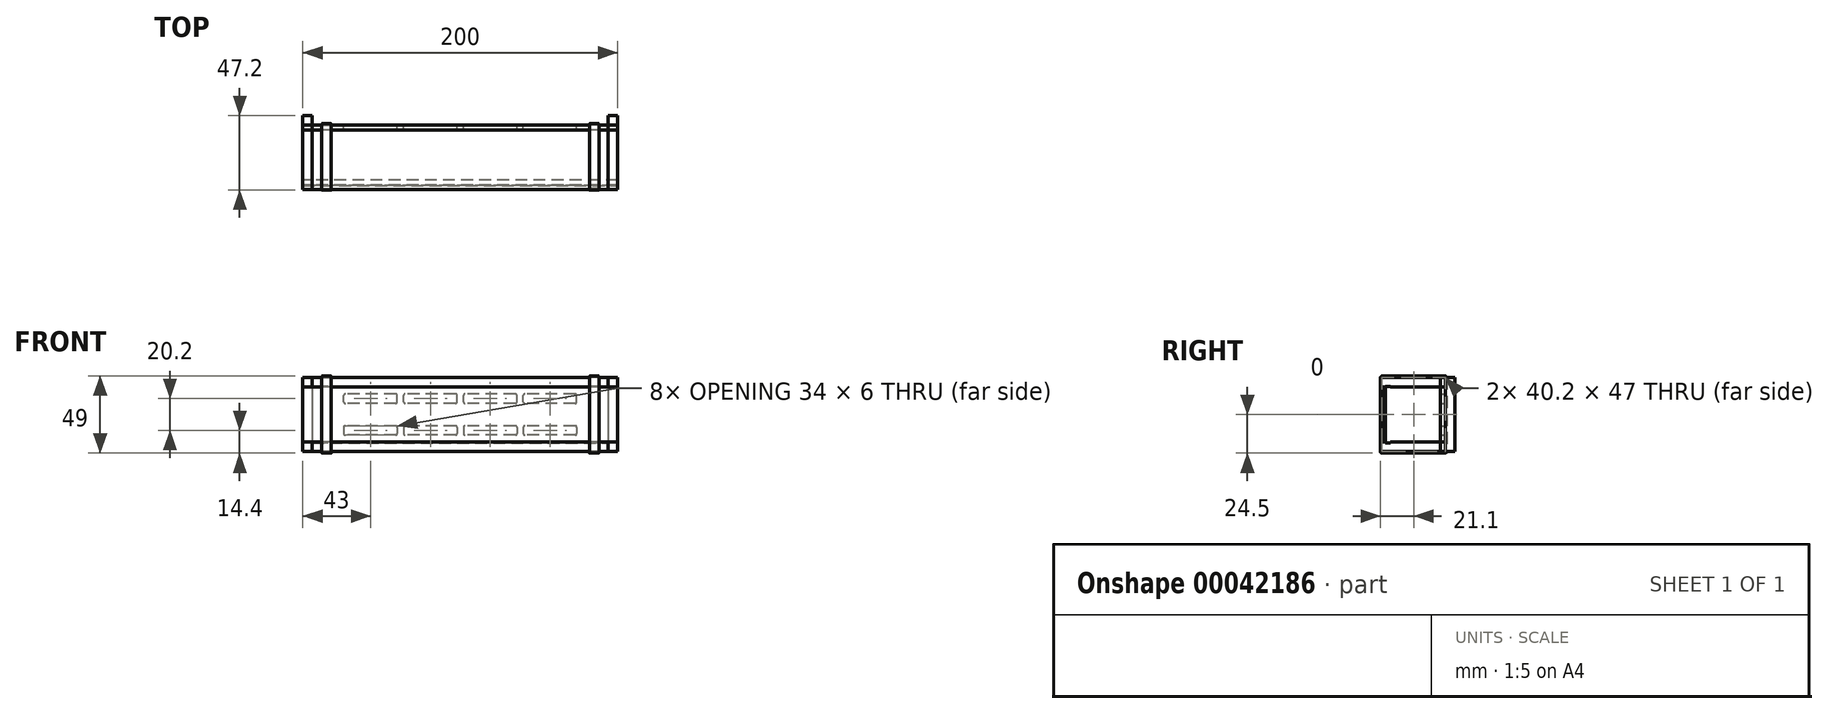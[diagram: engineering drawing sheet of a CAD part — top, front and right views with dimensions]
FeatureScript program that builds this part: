
annotation { "Feature Type Name" : "Feature", "Feature Type Description" : "" }
export const myFeature = defineFeature(function(context is Context, id is Id, definition is map)
    precondition{}
    {
        {
            var Q0;
            Q0=qCreatedBy(makeId("Front.planeOp"),FACE);
            var sketch = newSketch(context, id + "F0", { "sketchPlane" : qUnion([Q0])});
            skLineSegment(sketch, "E0.rect.bottom", {"start": v(100, 18) * mm, "end": v(-100, 18) * mm});
            skLineSegment(sketch, "E0.rect.top", {"start": v(100, -18) * mm, "end": v(-100, -18) * mm});
            skLineSegment(sketch, "E0.rect.left", {"start": v(100, 18) * mm, "end": v(100, -18) * mm});
            skLineSegment(sketch, "E0.rect.right", {"start": v(-100, 18) * mm, "end": v(-100, -18) * mm});
            skPoint(sketch, "E0.rect.middle", {"position": v(0, 0) * mm});
            skSolve(sketch);
        }
        {
            var Q0;
            Q0=qCreatedBy(makeId("Front.planeOp"),FACE);
            var sketch = newSketch(context, id + "F1", { "sketchPlane" : qUnion([Q0])});
            skLineSegment(sketch, "E1", {"start": v(38, 18) * mm, "end": v(38, -18) * mm, "construction": true});
            skLineSegment(sketch, "E2", {"start": v(0, 18) * mm, "end": v(38, -18) * mm, "construction": true});
            skLineSegment(sketch, "E3.rect.bottom", {"start": v(37, 12.5) * mm, "end": v(1, 12.5) * mm});
            skLineSegment(sketch, "E3.rect.top", {"start": v(37, -12.5) * mm, "end": v(1, -12.5) * mm});
            skLineSegment(sketch, "E3.rect.left", {"start": v(37, 12.5) * mm, "end": v(37, -12.5) * mm});
            skLineSegment(sketch, "E3.rect.right", {"start": v(1, 12.5) * mm, "end": v(1, -12.5) * mm});
            skPoint(sketch, "E3.rect.middle", {"position": v(19, 0) * mm});
            skLineSegment(sketch, "E4.1.0.0", {"start": v(75, 12.5) * mm, "end": v(39, 12.5) * mm});
            skLineSegment(sketch, "E4.1.0.1", {"start": v(39, 12.5) * mm, "end": v(39, -12.5) * mm});
            skLineSegment(sketch, "E4.1.0.2", {"start": v(75, -12.5) * mm, "end": v(39, -12.5) * mm});
            skLineSegment(sketch, "E4.1.0.3", {"start": v(75, 12.5) * mm, "end": v(75, -12.5) * mm});
            skLineSegment(sketch, "E4.direction1", {"start": v(1, 12.5) * mm, "end": v(39, 12.5) * mm, "construction": true});
            skLineSegment(sketch, "E5", {"start": v(0, 18) * mm, "end": v(0, -18) * mm, "construction": true});
            skLineSegment(sketch, "E6.1.0.0", {"start": v(-1, 12.5) * mm, "end": v(-37, 12.5) * mm});
            skLineSegment(sketch, "E6.1.0.1", {"start": v(-37, 12.5) * mm, "end": v(-37, -12.5) * mm});
            skLineSegment(sketch, "E6.1.0.2", {"start": v(-1, -12.5) * mm, "end": v(-37, -12.5) * mm});
            skLineSegment(sketch, "E6.1.0.3", {"start": v(-1, 12.5) * mm, "end": v(-1, -12.5) * mm});
            skLineSegment(sketch, "E6.2.0.0", {"start": v(-39, 12.5) * mm, "end": v(-75, 12.5) * mm});
            skLineSegment(sketch, "E6.2.0.1", {"start": v(-75, 12.5) * mm, "end": v(-75, -12.5) * mm});
            skLineSegment(sketch, "E6.2.0.2", {"start": v(-39, -12.5) * mm, "end": v(-75, -12.5) * mm});
            skLineSegment(sketch, "E6.2.0.3", {"start": v(-39, 12.5) * mm, "end": v(-39, -12.5) * mm});
            skLineSegment(sketch, "E6.direction1", {"start": v(1, 12.5) * mm, "end": v(-37, 12.5) * mm, "construction": true});
            skSolve(sketch);
        }
        {
            var Q0;
            Q0=qCreatedBy(makeId("Right.planeOp"),FACE);
            var sketch = newSketch(context, id + "F2", { "sketchPlane" : qUnion([Q0])});
            skLineSegment(sketch, "E7.bottom", {"start": v(0, 18) * mm, "end": v(3.17, 18) * mm});
            skLineSegment(sketch, "E7.top", {"start": v(0, -18) * mm, "end": v(3.18, -18) * mm});
            skLineSegment(sketch, "E7.left", {"start": v(0, 18) * mm, "end": v(0, -18) * mm});
            skLineSegment(sketch, "E7.right", {"start": v(3.17, 18) * mm, "end": v(3.18, -18) * mm});
            skSolve(sketch);
        }
        {
            var Q0;
            Q0=qCreatedBy(makeId("Right.planeOp"),FACE);
            var sketch = newSketch(context, id + "F3", { "sketchPlane" : qUnion([Q0])});
            skLineSegment(sketch, "E8", {"start": v(-3, 17.5) * mm, "end": v(-3, 23.5) * mm});
            skLineSegment(sketch, "E9", {"start": v(-3, 23.5) * mm, "end": v(44, 23.5) * mm});
            skLineSegment(sketch, "E10", {"start": v(44, 23.5) * mm, "end": v(44, -23.5) * mm});
            skLineSegment(sketch, "E11", {"start": v(44, -23.5) * mm, "end": v(-3, -23.5) * mm});
            skLineSegment(sketch, "E12", {"start": v(-3, -23.5) * mm, "end": v(-3, -17.5) * mm});
            skLineSegment(sketch, "E13", {"start": v(-3, 17.5) * mm, "end": v(0, 17.5) * mm});
            skLineSegment(sketch, "E14", {"start": v(0, 17.5) * mm, "end": v(0, 18) * mm});
            skLineSegment(sketch, "E15", {"start": v(0, 18) * mm, "end": v(3.17, 18) * mm});
            skLineSegment(sketch, "E16", {"start": v(3.17, 18) * mm, "end": v(3.18, -18) * mm});
            skLineSegment(sketch, "E17", {"start": v(3.18, -18) * mm, "end": v(0, -18) * mm});
            skLineSegment(sketch, "E18", {"start": v(0, -18) * mm, "end": v(0, -17.5) * mm});
            skLineSegment(sketch, "E19", {"start": v(0, -17.5) * mm, "end": v(-3, -17.5) * mm});
            skLineSegment(sketch, "E20", {"start": v(0, 0) * mm, "end": v(44, 0) * mm, "construction": true});
            skPoint(sketch, "E20.endSnap0", {"position": v(44, 0) * mm});
            skSolve(sketch);
        }
        {
            var Q0;
            Q0=qCreatedBy(makeId("Right.planeOp"),FACE);
            var sketch = newSketch(context, id + "F4", { "sketchPlane" : qUnion([Q0])});
            skLineSegment(sketch, "E21.bottom", {"start": v(38, 17.5) * mm, "end": v(3.18, 17.5) * mm});
            skLineSegment(sketch, "E21.top", {"start": v(38, 23.5) * mm, "end": v(-3, 23.5) * mm});
            skLineSegment(sketch, "E21.left", {"start": v(38, 17.5) * mm, "end": v(38, 23.5) * mm});
            skLineSegment(sketch, "E21.right", {"start": v(-3, 17.5) * mm, "end": v(-3, 23.5) * mm});
            skLineSegment(sketch, "E22", {"start": v(0, 17.5) * mm, "end": v(0, 18) * mm});
            skLineSegment(sketch, "E23", {"start": v(0, 18) * mm, "end": v(3.17, 18) * mm});
            skLineSegment(sketch, "E24", {"start": v(3.17, 18) * mm, "end": v(3.17, 17.5) * mm});
            skLineSegment(sketch, "E25.trimOffspring", {"start": v(0, 17.5) * mm, "end": v(-3, 17.5) * mm});
            skLineSegment(sketch, "E26.bottom", {"start": v(-3, -17.5) * mm, "end": v(0, -17.5) * mm});
            skLineSegment(sketch, "E26.top", {"start": v(-3, -23.5) * mm, "end": v(38, -23.5) * mm});
            skLineSegment(sketch, "E26.left", {"start": v(-3, -17.5) * mm, "end": v(-3, -23.5) * mm});
            skLineSegment(sketch, "E26.right", {"start": v(38, -17.5) * mm, "end": v(38, -23.5) * mm});
            skLineSegment(sketch, "E27.top", {"start": v(3.18, -18) * mm, "end": v(0, -18) * mm});
            skLineSegment(sketch, "E27.left", {"start": v(3.18, -17.5) * mm, "end": v(3.18, -18) * mm});
            skLineSegment(sketch, "E27.right", {"start": v(0, -17.5) * mm, "end": v(0, -18) * mm});
            skLineSegment(sketch, "E28.trimOffspring", {"start": v(3.18, -17.5) * mm, "end": v(38, -17.5) * mm});
            skSolve(sketch);
        }
        {
            var Q0;
            Q0=qCreatedBy(makeId("Right.planeOp"),FACE);
            var Q1;
            Q1=sQuery(id+"F0.wireOp",VERTEX,"E0.rect.bottom.start");
            cPlane(context, id + "F5", {"entities" : qUnion([Q0, Q1]), "cplaneType" : CPlaneType.PLANE_POINT, "offset" : 150 * mm, "width" : 150 * mm, "height" : 150 * mm});
        }
        {
            var Q0;
            Q0=qCreatedBy(makeId("Right.planeOp"),FACE);
            var Q1;
            Q1=sQuery(id+"F0.wireOp",VERTEX,"E0.rect.right.start");
            cPlane(context, id + "F6", {"entities" : qUnion([Q0, Q1]), "cplaneType" : CPlaneType.PLANE_POINT, "offset" : 150 * mm, "width" : 150 * mm, "height" : 150 * mm});
        }
        {
            var Q0;
            Q0 = qSketchRegion(id + "F4", true);
            var Q1;
            Q1=qCreatedBy(id+"F5.planeOp",FACE);
            var Q2;
            Q2=qCreatedBy(id+"F6.planeOp",FACE);
            extrude(context, id + "F7", {"entities" : qUnion([Q0]), "endBound" : BoundingType.UP_TO_SURFACE, "endBoundEntityFace" : qUnion([Q1]), "depth" : 25 * mm, "hasSecondDirection" : true, "secondDirectionBound" : SecondDirectionBoundingType.UP_TO_SURFACE, "secondDirectionOppositeDirection" : true, "secondDirectionBoundEntityFace" : qUnion([Q2]), "secondDirectionDepth" : 25 * mm});
        }
        {
            var Q0;
            Q0=qCreatedBy(id+"F5.planeOp",FACE);
            var sketch = newSketch(context, id + "F8", { "sketchPlane" : qUnion([Q0])});
            skLineSegment(sketch, "E29.0", {"start": v(-3, 17.5) * mm, "end": v(-3, 23.5) * mm});
            skLineSegment(sketch, "E29.1", {"start": v(-3, 23.5) * mm, "end": v(44, 23.5) * mm});
            skLineSegment(sketch, "E29.2", {"start": v(44, 23.5) * mm, "end": v(44, -23.5) * mm});
            skLineSegment(sketch, "E29.3", {"start": v(44, -23.5) * mm, "end": v(-3, -23.5) * mm});
            skLineSegment(sketch, "E29.4", {"start": v(-3, -23.5) * mm, "end": v(-3, -17.5) * mm});
            skLineSegment(sketch, "E29.5", {"start": v(-3, 17.5) * mm, "end": v(0, 17.5) * mm});
            skLineSegment(sketch, "E29.11", {"start": v(0, -17.5) * mm, "end": v(-3, -17.5) * mm});
            skLineSegment(sketch, "E30", {"start": v(0, 17.5) * mm, "end": v(0, -17.5) * mm});
            skSolve(sketch);
        }
        {
            var Q0;
            Q0 = qSketchRegion(id + "F8", true);
            extrude(context, id + "F9", {"entities" : qUnion([Q0]), "oppositeDirection" : true, "depth" : 6 * mm});
        }
        {
            var Q0;
            Q0=qCreatedBy(id+"F6.planeOp",FACE);
            var sketch = newSketch(context, id + "F10", { "sketchPlane" : qUnion([Q0])});
            skLineSegment(sketch, "E31.0", {"start": v(-3, 17.5) * mm, "end": v(-3, 23.5) * mm});
            skLineSegment(sketch, "E31.1", {"start": v(-3, 23.5) * mm, "end": v(44, 23.5) * mm});
            skLineSegment(sketch, "E31.2", {"start": v(44, 23.5) * mm, "end": v(44, -23.5) * mm});
            skLineSegment(sketch, "E31.3", {"start": v(44, -23.5) * mm, "end": v(-3, -23.5) * mm});
            skLineSegment(sketch, "E31.4", {"start": v(-3, -23.5) * mm, "end": v(-3, -17.5) * mm});
            skLineSegment(sketch, "E31.5", {"start": v(-3, 17.5) * mm, "end": v(0, 17.5) * mm});
            skLineSegment(sketch, "E31.11", {"start": v(0, -17.5) * mm, "end": v(-3, -17.5) * mm});
            skLineSegment(sketch, "E32", {"start": v(0, 17.5) * mm, "end": v(0, -17.5) * mm});
            skSolve(sketch);
        }
        {
            var Q0;
            Q0 = qSketchRegion(id + "F10", true);
            extrude(context, id + "F11", {"entities" : qUnion([Q0]), "depth" : 6 * mm});
        }
        {
            var Q0;
            Q0=qCreatedBy(makeId("Front.planeOp"),FACE);
            var sketch = newSketch(context, id + "F12", { "sketchPlane" : qUnion([Q0])});
            skLineSegment(sketch, "E33.bottom", {"start": v(-94, 18) * mm, "end": v(94, 18) * mm});
            skLineSegment(sketch, "E33.top", {"start": v(-94, -18) * mm, "end": v(94, -18) * mm});
            skLineSegment(sketch, "E33.left", {"start": v(-94, 18) * mm, "end": v(-94, -18) * mm});
            skLineSegment(sketch, "E33.right", {"start": v(94, 18) * mm, "end": v(94, -18) * mm});
            skSolve(sketch);
        }
        {
            var Q0;
            Q0 = qSketchRegion(id + "F12", true);
            extrude(context, id + "F13", {"entities" : qUnion([Q0]), "oppositeDirection" : true, "depth" : 1 / 203.2 * mm});
        }
        {
            var Q0;
            Q0=makeQuery(id+"F7.opExtrude","SWEPT_FACE",FACE,{"disambiguationData":[OSD([sQuery(id+"F4.wireOp",EDGE,"E21.left")])]});
            var sketch = newSketch(context, id + "F14", { "sketchPlane" : qUnion([Q0])});
            skLineSegment(sketch, "E34.bottom", {"start": v(100, 23.5) * mm, "end": v(-100, 23.5) * mm});
            skLineSegment(sketch, "E34.top", {"start": v(100, -23.5) * mm, "end": v(-100, -23.5) * mm});
            skLineSegment(sketch, "E34.left", {"start": v(100, 23.5) * mm, "end": v(100, -23.5) * mm});
            skLineSegment(sketch, "E34.right", {"start": v(-100, 23.5) * mm, "end": v(-100, -23.5) * mm});
            skSolve(sketch);
        }
        {
            var Q0;
            Q0 = qSketchRegion(id + "F14", true);
            extrude(context, id + "F15", {"entities" : qUnion([Q0]), "oppositeDirection" : true, "depth" : 3 * mm});
        }
        {
            var Q0;
            Q0=makeQuery(id+"F15.opExtrude","CAP_FACE",FACE,{"disambiguationData":[OSD([sQuery(id+"F14.wireOp",EDGE,"E34.bottom"),sQuery(id+"F14.wireOp",EDGE,"E34.top"),sQuery(id+"F14.wireOp",EDGE,"E34.left"),sQuery(id+"F14.wireOp",EDGE,"E34.right")])],"isStart":true});
            var sketch = newSketch(context, id + "F16", { "sketchPlane" : qUnion([Q0])});
            skLineSegment(sketch, "E35", {"start": v(-19, 10.1) * mm, "end": v(-19, 0) * mm, "construction": true});
            skLineSegment(sketch, "E36.rect.bottom", {"start": v(-35, 7.1) * mm, "end": v(-3, 7.1) * mm});
            skLineSegment(sketch, "E36.rect.top", {"start": v(-35, 13.1) * mm, "end": v(-3, 13.1) * mm});
            skLineSegment(sketch, "E36.rect.left", {"start": v(-36, 8.1) * mm, "end": v(-36, 12.1) * mm});
            skLineSegment(sketch, "E36.rect.right", {"start": v(-2, 8.1) * mm, "end": v(-2, 12.1) * mm});
            skPoint(sketch, "E36.rect.middle", {"position": v(-19, 10.1) * mm});
            skLineSegment(sketch, "E37.rect.bottom", {"start": v(0, 4) * mm, "end": v(-38, 4) * mm, "construction": true});
            skLineSegment(sketch, "E37.rect.top", {"start": v(0, -4) * mm, "end": v(-38, -4) * mm, "construction": true});
            skLineSegment(sketch, "E37.rect.left", {"start": v(0, 4) * mm, "end": v(0, -4) * mm, "construction": true});
            skLineSegment(sketch, "E37.rect.right", {"start": v(-38, 4) * mm, "end": v(-38, -4) * mm, "construction": true});
            skPoint(sketch, "E37.rect.middle", {"position": v(-19, 0) * mm});
            skLineSegment(sketch, "E38", {"start": v(0, 16.2) * mm, "end": v(-38, 4) * mm, "construction": true});
            skLineSegment(sketch, "E39", {"start": v(0, 0) * mm, "end": v(-38, 0) * mm, "construction": true});
            skPoint(sketch, "E40.visualSharp", {"position": v(-2, 13.1) * mm});
            skArc(sketch, "E40.filletArc", {"start": v(-2, 12.1) * mm, "mid": v(-2.3, 12.8) * mm, "end": v(-3, 13.1) * mm});
            skPoint(sketch, "E41.visualSharp", {"position": v(-2, 7.1) * mm});
            skArc(sketch, "E41.filletArc", {"start": v(-3, 7.1) * mm, "mid": v(-2.3, 7.4) * mm, "end": v(-2, 8.1) * mm});
            skPoint(sketch, "E42.visualSharp", {"position": v(-36, 13.1) * mm});
            skArc(sketch, "E42.filletArc", {"start": v(-35, 13.1) * mm, "mid": v(-35.7, 12.8) * mm, "end": v(-36, 12.1) * mm});
            skPoint(sketch, "E43.visualSharp", {"position": v(-36, 7.1) * mm});
            skArc(sketch, "E43.filletArc", {"start": v(-36, 8.1) * mm, "mid": v(-35.7, 7.4) * mm, "end": v(-35, 7.1) * mm});
            skArc(sketch, "E44.MirrorCS", {"start": v(-2, -12.1) * mm, "mid": v(-2.3, -12.8) * mm, "end": v(-3, -13.1) * mm});
            skArc(sketch, "E45.MirrorCS", {"start": v(-35, -13.1) * mm, "mid": v(-35.7, -12.8) * mm, "end": v(-36, -12.1) * mm});
            skArc(sketch, "E46.MirrorCS", {"start": v(-36, -8.1) * mm, "mid": v(-35.7, -7.4) * mm, "end": v(-35, -7.1) * mm});
            skArc(sketch, "E47.MirrorCS", {"start": v(-3, -7.1) * mm, "mid": v(-2.3, -7.4) * mm, "end": v(-2, -8.1) * mm});
            skLineSegment(sketch, "E48.MirrorCS", {"start": v(-2, -8.1) * mm, "end": v(-2, -12.1) * mm});
            skLineSegment(sketch, "E49.MirrorCS", {"start": v(-35, -7.1) * mm, "end": v(-3, -7.1) * mm});
            skPoint(sketch, "E50.MirrorP", {"position": v(-19, -10.1) * mm});
            skLineSegment(sketch, "E51.MirrorCS", {"start": v(-36, -8.1) * mm, "end": v(-36, -12.1) * mm});
            skLineSegment(sketch, "E52.MirrorCS", {"start": v(-35, -13.1) * mm, "end": v(-3, -13.1) * mm});
            skPoint(sketch, "E53.MirrorP", {"position": v(-36, -7.1) * mm});
            skPoint(sketch, "E54.MirrorP", {"position": v(-2, -7.1) * mm});
            skPoint(sketch, "E55.MirrorP", {"position": v(-2, -13.1) * mm});
            skPoint(sketch, "E56.MirrorP", {"position": v(-36, -13.1) * mm});
            skPoint(sketch, "E57.1.0.0", {"position": v(36, 7.1) * mm});
            skPoint(sketch, "E57.1.0.1", {"position": v(2, 13.1) * mm});
            skPoint(sketch, "E57.1.0.2", {"position": v(36, 13.1) * mm});
            skPoint(sketch, "E57.1.0.3", {"position": v(2, 7.1) * mm});
            skLineSegment(sketch, "E57.1.0.4", {"start": v(3, 7.1) * mm, "end": v(35, 7.1) * mm});
            skLineSegment(sketch, "E57.1.0.5", {"start": v(3, 13.1) * mm, "end": v(35, 13.1) * mm});
            skLineSegment(sketch, "E57.1.0.6", {"start": v(2, 8.1) * mm, "end": v(2, 12.1) * mm});
            skPoint(sketch, "E57.1.0.7", {"position": v(19, 10.1) * mm});
            skLineSegment(sketch, "E57.1.0.8", {"start": v(36, 8.1) * mm, "end": v(36, 12.1) * mm});
            skArc(sketch, "E57.1.0.9", {"start": v(2, 8.1) * mm, "mid": v(2.3, 7.4) * mm, "end": v(3, 7.1) * mm});
            skArc(sketch, "E57.1.0.10", {"start": v(3, 13.1) * mm, "mid": v(2.3, 12.8) * mm, "end": v(2, 12.1) * mm});
            skArc(sketch, "E57.1.0.11", {"start": v(36, 12.1) * mm, "mid": v(35.7, 12.8) * mm, "end": v(35, 13.1) * mm});
            skArc(sketch, "E57.1.0.12", {"start": v(35, 7.1) * mm, "mid": v(35.7, 7.4) * mm, "end": v(36, 8.1) * mm});
            skPoint(sketch, "E57.1.0.13", {"position": v(19, -10.1) * mm});
            skPoint(sketch, "E57.1.0.14", {"position": v(2, -13.1) * mm});
            skPoint(sketch, "E57.1.0.15", {"position": v(2, -7.1) * mm});
            skPoint(sketch, "E57.1.0.16", {"position": v(36, -7.1) * mm});
            skPoint(sketch, "E57.1.0.17", {"position": v(36, -13.1) * mm});
            skLineSegment(sketch, "E57.1.0.18", {"start": v(36, -8.1) * mm, "end": v(36, -12.1) * mm});
            skLineSegment(sketch, "E57.1.0.19", {"start": v(3, -7.1) * mm, "end": v(35, -7.1) * mm});
            skLineSegment(sketch, "E57.1.0.20", {"start": v(3, -13.1) * mm, "end": v(35, -13.1) * mm});
            skLineSegment(sketch, "E57.1.0.21", {"start": v(2, -8.1) * mm, "end": v(2, -12.1) * mm});
            skLineSegment(sketch, "E57.1.0.22", {"start": v(3, -13.1) * mm, "end": v(35, -13.1) * mm});
            skArc(sketch, "E57.1.0.23", {"start": v(2, -8.1) * mm, "mid": v(2.3, -7.4) * mm, "end": v(3, -7.1) * mm});
            skArc(sketch, "E57.1.0.24", {"start": v(35, -7.1) * mm, "mid": v(35.7, -7.4) * mm, "end": v(36, -8.1) * mm});
            skArc(sketch, "E57.1.0.25", {"start": v(36, -12.1) * mm, "mid": v(35.7, -12.8) * mm, "end": v(35, -13.1) * mm});
            skArc(sketch, "E57.1.0.26", {"start": v(3, -13.1) * mm, "mid": v(2.3, -12.8) * mm, "end": v(2, -12.1) * mm});
            skPoint(sketch, "E57.2.0.0", {"position": v(74, 7.1) * mm});
            skPoint(sketch, "E57.2.0.1", {"position": v(40, 13.1) * mm});
            skPoint(sketch, "E57.2.0.2", {"position": v(74, 13.1) * mm});
            skPoint(sketch, "E57.2.0.3", {"position": v(40, 7.1) * mm});
            skLineSegment(sketch, "E57.2.0.4", {"start": v(41, 7.1) * mm, "end": v(73, 7.1) * mm});
            skLineSegment(sketch, "E57.2.0.5", {"start": v(41, 13.1) * mm, "end": v(73, 13.1) * mm});
            skLineSegment(sketch, "E57.2.0.6", {"start": v(40, 8.1) * mm, "end": v(40, 12.1) * mm});
            skPoint(sketch, "E57.2.0.7", {"position": v(57, 10.1) * mm});
            skLineSegment(sketch, "E57.2.0.8", {"start": v(74, 8.1) * mm, "end": v(74, 12.1) * mm});
            skArc(sketch, "E57.2.0.9", {"start": v(40, 8.1) * mm, "mid": v(40.3, 7.4) * mm, "end": v(41, 7.1) * mm});
            skArc(sketch, "E57.2.0.10", {"start": v(41, 13.1) * mm, "mid": v(40.3, 12.8) * mm, "end": v(40, 12.1) * mm});
            skArc(sketch, "E57.2.0.11", {"start": v(74, 12.1) * mm, "mid": v(73.7, 12.8) * mm, "end": v(73, 13.1) * mm});
            skArc(sketch, "E57.2.0.12", {"start": v(73, 7.1) * mm, "mid": v(73.7, 7.4) * mm, "end": v(74, 8.1) * mm});
            skPoint(sketch, "E57.2.0.13", {"position": v(57, -10.1) * mm});
            skPoint(sketch, "E57.2.0.14", {"position": v(40, -13.1) * mm});
            skPoint(sketch, "E57.2.0.15", {"position": v(40, -7.1) * mm});
            skPoint(sketch, "E57.2.0.16", {"position": v(74, -7.1) * mm});
            skPoint(sketch, "E57.2.0.17", {"position": v(74, -13.1) * mm});
            skLineSegment(sketch, "E57.2.0.18", {"start": v(74, -8.1) * mm, "end": v(74, -12.1) * mm});
            skLineSegment(sketch, "E57.2.0.19", {"start": v(41, -7.1) * mm, "end": v(73, -7.1) * mm});
            skLineSegment(sketch, "E57.2.0.20", {"start": v(41, -13.1) * mm, "end": v(73, -13.1) * mm});
            skLineSegment(sketch, "E57.2.0.21", {"start": v(40, -8.1) * mm, "end": v(40, -12.1) * mm});
            skLineSegment(sketch, "E57.2.0.22", {"start": v(41, -13.1) * mm, "end": v(73, -13.1) * mm});
            skArc(sketch, "E57.2.0.23", {"start": v(40, -8.1) * mm, "mid": v(40.3, -7.4) * mm, "end": v(41, -7.1) * mm});
            skArc(sketch, "E57.2.0.24", {"start": v(73, -7.1) * mm, "mid": v(73.7, -7.4) * mm, "end": v(74, -8.1) * mm});
            skArc(sketch, "E57.2.0.25", {"start": v(74, -12.1) * mm, "mid": v(73.7, -12.8) * mm, "end": v(73, -13.1) * mm});
            skArc(sketch, "E57.2.0.26", {"start": v(41, -13.1) * mm, "mid": v(40.3, -12.8) * mm, "end": v(40, -12.1) * mm});
            skLineSegment(sketch, "E57.direction1", {"start": v(-2, 7.1) * mm, "end": v(36, 7.1) * mm, "construction": true});
            skPoint(sketch, "E58.1.0.0", {"position": v(-74, 13.1) * mm});
            skPoint(sketch, "E58.1.0.1", {"position": v(-74, -7.1) * mm});
            skPoint(sketch, "E58.1.0.2", {"position": v(-57, -10.1) * mm});
            skPoint(sketch, "E58.1.0.3", {"position": v(-74, 7.1) * mm});
            skPoint(sketch, "E58.1.0.4", {"position": v(-40, 7.1) * mm});
            skLineSegment(sketch, "E58.1.0.5", {"start": v(-73, -7.1) * mm, "end": v(-41, -7.1) * mm});
            skPoint(sketch, "E58.1.0.6", {"position": v(-40, -7.1) * mm});
            skPoint(sketch, "E58.1.0.7", {"position": v(-57, 10.1) * mm});
            skLineSegment(sketch, "E58.1.0.8", {"start": v(-73, 7.1) * mm, "end": v(-41, 7.1) * mm});
            skLineSegment(sketch, "E58.1.0.9", {"start": v(-73, 13.1) * mm, "end": v(-41, 13.1) * mm});
            skLineSegment(sketch, "E58.1.0.10", {"start": v(-74, 8.1) * mm, "end": v(-74, 12.1) * mm});
            skPoint(sketch, "E58.1.0.11", {"position": v(-40, -13.1) * mm});
            skLineSegment(sketch, "E58.1.0.12", {"start": v(-73, -13.1) * mm, "end": v(-41, -13.1) * mm});
            skPoint(sketch, "E58.1.0.13", {"position": v(-74, -13.1) * mm});
            skPoint(sketch, "E58.1.0.14", {"position": v(-40, 13.1) * mm});
            skLineSegment(sketch, "E58.1.0.15", {"start": v(-73, -13.1) * mm, "end": v(-41, -13.1) * mm});
            skLineSegment(sketch, "E58.1.0.16", {"start": v(-40, -8.1) * mm, "end": v(-40, -12.1) * mm});
            skLineSegment(sketch, "E58.1.0.17", {"start": v(-74, -8.1) * mm, "end": v(-74, -12.1) * mm});
            skArc(sketch, "E58.1.0.18", {"start": v(-73, 13.1) * mm, "mid": v(-73.7, 12.8) * mm, "end": v(-74, 12.1) * mm});
            skLineSegment(sketch, "E58.1.0.19", {"start": v(-40, 8.1) * mm, "end": v(-40, 12.1) * mm});
            skArc(sketch, "E58.1.0.20", {"start": v(-74, -8.1) * mm, "mid": v(-73.7, -7.4) * mm, "end": v(-73, -7.1) * mm});
            skArc(sketch, "E58.1.0.21", {"start": v(-74, 8.1) * mm, "mid": v(-73.7, 7.4) * mm, "end": v(-73, 7.1) * mm});
            skArc(sketch, "E58.1.0.22", {"start": v(-40, -12.1) * mm, "mid": v(-40.3, -12.8) * mm, "end": v(-41, -13.1) * mm});
            skArc(sketch, "E58.1.0.23", {"start": v(-41, 7.1) * mm, "mid": v(-40.3, 7.4) * mm, "end": v(-40, 8.1) * mm});
            skArc(sketch, "E58.1.0.24", {"start": v(-73, -13.1) * mm, "mid": v(-73.7, -12.8) * mm, "end": v(-74, -12.1) * mm});
            skArc(sketch, "E58.1.0.25", {"start": v(-41, -7.1) * mm, "mid": v(-40.3, -7.4) * mm, "end": v(-40, -8.1) * mm});
            skArc(sketch, "E58.1.0.26", {"start": v(-40, 12.1) * mm, "mid": v(-40.3, 12.8) * mm, "end": v(-41, 13.1) * mm});
            skLineSegment(sketch, "E58.direction1", {"start": v(-36, 13.1) * mm, "end": v(-74, 13.1) * mm, "construction": true});
            skSolve(sketch);
        }
        {
            var Q0;
            Q0 = qSketchRegion(id + "F16", true);
            extrude(context, id + "F17", {"entities" : qUnion([Q0]), "operationType" : NewBodyOperationType.REMOVE, "oppositeDirection" : true, "depth" : 10 * mm});
        }
        {
            var Q0;
            Q0=makeQuery(id+"F13.opExtrude","CAP_FACE",FACE,{"disambiguationData":[OSD([sQuery(id+"F12.wireOp",EDGE,"E33.bottom"),sQuery(id+"F12.wireOp",EDGE,"E33.top"),sQuery(id+"F12.wireOp",EDGE,"E33.left"),sQuery(id+"F12.wireOp",EDGE,"E33.right")])],"isStart":true});
            cPlane(context, id + "F18", {"entities" : qUnion([Q0]), "cplaneType" : CPlaneType.OFFSET, "offset" : .2 * mm, "width" : 150 * mm, "height" : 150 * mm});
        }
        {
            var Q0;
            Q0=qCreatedBy(id+"F18.planeOp",FACE);
            var sketch = newSketch(context, id + "F19", { "sketchPlane" : qUnion([Q0])});
            skLineSegment(sketch, "E59.bottom", {"start": v(-100, 17.5) * mm, "end": v(100, 17.5) * mm});
            skLineSegment(sketch, "E59.top", {"start": v(-100, -17.5) * mm, "end": v(100, -17.5) * mm});
            skLineSegment(sketch, "E59.left", {"start": v(-100, 17.5) * mm, "end": v(-100, -17.5) * mm});
            skLineSegment(sketch, "E59.right", {"start": v(100, 17.5) * mm, "end": v(100, -17.5) * mm});
            skSolve(sketch);
        }
        {
            var Q0;
            Q0 = qSketchRegion(id + "F19", true);
            extrude(context, id + "F20", {"entities" : qUnion([Q0]), "depth" : 2 * mm});
        }
        {
            var Q0;
            Q0=makeQuery(id+"F20.opExtrude","CAP_FACE",FACE,{"disambiguationData":[OSD([sQuery(id+"F19.wireOp",EDGE,"E59.bottom"),sQuery(id+"F19.wireOp",EDGE,"E59.top"),sQuery(id+"F19.wireOp",EDGE,"E59.left"),sQuery(id+"F19.wireOp",EDGE,"E59.right")])],"isStart":false});
            var sketch = newSketch(context, id + "F21", { "sketchPlane" : qUnion([Q0])});
            skLineSegment(sketch, "E60", {"start": v(0, 17.5) * mm, "end": v(76, -17.5) * mm, "construction": true});
            skPoint(sketch, "E61", {"position": v(38, 0) * mm});
            skLineSegment(sketch, "E62", {"start": v(76, -17.5) * mm, "end": v(94, 17.5) * mm, "construction": true});
            skPoint(sketch, "E63", {"position": v(85, 0) * mm});
            skSolve(sketch);
        }
        {
            var Q0;
            Q0=qCreatedBy(makeId("Right.planeOp"),FACE);
            var Q1;
            Q1=sQuery(id+"F21.wireOp",VERTEX,"E63");
            cPlane(context, id + "F22", {"entities" : qUnion([Q0, Q1]), "cplaneType" : CPlaneType.PLANE_POINT, "offset" : 150 * mm, "width" : 150 * mm, "height" : 150 * mm});
        }
        {
            var Q0;
            Q0=qCreatedBy(id+"F22.planeOp",FACE);
            var sketch = newSketch(context, id + "F23", { "sketchPlane" : qUnion([Q0])});
            skLineSegment(sketch, "E64.bottom", {"start": v(-2.2, 23.5) * mm, "end": v(38, 23.5) * mm});
            skLineSegment(sketch, "E64.top", {"start": v(-2.2, -23.5) * mm, "end": v(38, -23.5) * mm});
            skLineSegment(sketch, "E64.left", {"start": v(-2.2, 23.5) * mm, "end": v(-2.2, -23.5) * mm});
            skLineSegment(sketch, "E64.right", {"start": v(38, 23.5) * mm, "end": v(38, -23.5) * mm});
            skLineSegment(sketch, "E65.0", {"start": v(-2.05, -24.5) * mm, "end": v(37.85, -24.5) * mm});
            skLineSegment(sketch, "E65.1", {"start": v(-3.2, 23.35) * mm, "end": v(-3.2, -23.35) * mm});
            skLineSegment(sketch, "E65.2", {"start": v(-2.05, 24.5) * mm, "end": v(37.85, 24.5) * mm});
            skLineSegment(sketch, "E65.3", {"start": v(39, 23.35) * mm, "end": v(39, -23.35) * mm});
            skPoint(sketch, "E66.visualSharp", {"position": v(-3.2, 24.5) * mm});
            skArc(sketch, "E66.filletArc", {"start": v(-2.05, 24.5) * mm, "mid": v(-2.86, 24.16) * mm, "end": v(-3.2, 23.35) * mm});
            skPoint(sketch, "E67.visualSharp", {"position": v(39, 24.5) * mm});
            skArc(sketch, "E67.filletArc", {"start": v(39, 23.35) * mm, "mid": v(38.66, 24.16) * mm, "end": v(37.85, 24.5) * mm});
            skPoint(sketch, "E68.visualSharp", {"position": v(39, -24.5) * mm});
            skArc(sketch, "E68.filletArc", {"start": v(37.85, -24.5) * mm, "mid": v(38.66, -24.16) * mm, "end": v(39, -23.35) * mm});
            skPoint(sketch, "E69.visualSharp", {"position": v(-3.2, -24.5) * mm});
            skArc(sketch, "E69.filletArc", {"start": v(-3.2, -23.35) * mm, "mid": v(-2.86, -24.16) * mm, "end": v(-2.05, -24.5) * mm});
            skSolve(sketch);
        }
        {
            var Q0;
            Q0=makeQuery(id+"F23.imprint","IMPRINT",FACE,{"disambiguationData":[TD([[makeQuery(id+"F23.imprint","IMPRINT",EDGE,{"derivedFrom":sQuery(id+"F23.wireOp",EDGE,"E64.bottom")}),1.0]])]});
            extrude(context, id + "F24", {"entities" : qUnion([Q0]), "endBound" : BoundingType.SYMMETRIC, "depth" : 6 * mm});
        }
        {
            var Q0;
            Q0=makeQuery(id+"F24.opExtrude","SWEPT_BODY",BODY,{"disambiguationData":[OSD([sQuery(id+"F23.wireOp",EDGE,"E64.bottom"),sQuery(id+"F23.wireOp",EDGE,"E64.top"),sQuery(id+"F23.wireOp",EDGE,"E64.left"),sQuery(id+"F23.wireOp",EDGE,"E64.right"),sQuery(id+"F23.wireOp",EDGE,"E65.0"),sQuery(id+"F23.wireOp",EDGE,"E65.1"),sQuery(id+"F23.wireOp",EDGE,"E65.2"),sQuery(id+"F23.wireOp",EDGE,"E65.3"),sQuery(id+"F23.wireOp",EDGE,"E66.filletArc"),sQuery(id+"F23.wireOp",EDGE,"E67.filletArc"),sQuery(id+"F23.wireOp",EDGE,"E68.filletArc"),sQuery(id+"F23.wireOp",EDGE,"E69.filletArc")])]});
            var Q1;
            Q1=qCreatedBy(makeId("Right.planeOp"),FACE);
            mirror(context, id + "F25", {"entities" : qUnion([Q0]), "mirrorPlane" : qUnion([Q1])});
        }
    });
